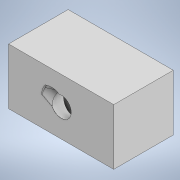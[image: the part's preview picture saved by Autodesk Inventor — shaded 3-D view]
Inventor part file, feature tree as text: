
AUTODESK INVENTOR PART (.ipt)
format: ipt  version: 2022 (Build 260153000, 153)  size: 832,000 bytes
history: native  units: mm
features: extrude x4, sketch x4, boolean_combine x1
ambient origin geometry x8: Origin, YZ Plane, XZ Plane, XY Plane, X Axis, Y Axis, Z Axis, Center Point
bodies: Solid1 (feature_tree), Solid6 (feature_tree)
feature tree (9):
  extrude  "Extrusion4"  Depth=8.0mm
  boolean_combine  "Combine3"
  extrude  "Extrusion6"  Depth=30.0mm
  extrude  "Extrusion7"  Depth=6.0mm
  extrude  "Extrusion8"  Depth=3.0mm TaperAngle=0.0deg
  sketch  "Sketch4"  dims[d21=8.0mm d22=8.0mm]
  sketch  "Sketch7"  dims[d23=15.0mm d24=30.0mm]
  sketch  "Sketch11"  dims[d25=20.0mm d26=0.0mm d31=6.0mm]
  sketch  "Sketch12"  dims[d32=1.0mm d33=0.0mm d35=3.0mm d36=0.0mm d37=0.0mm d38=0.0mm]
